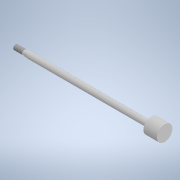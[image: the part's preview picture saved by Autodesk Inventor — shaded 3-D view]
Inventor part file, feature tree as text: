
AUTODESK INVENTOR PART (.ipt)
format: ipt  version: 2024.3 (Build 283343000, 343)  size: 141,824 bytes
history: native  units: mm
features: other x14, sketch x2, revolve x1, thread x1, extrude x1
ambient origin geometry x8: Origin, YZ Plane, XZ Plane, XY Plane, X Axis, Y Axis, Z Axis, Center Point
bodies: Solid1 (feature_tree)
feature tree (19):
  revolve  "Revolution1"  [1 undecoded]
  thread  "Thread1"  [1 undecoded]
  extrude  "Extrusion1"  [1 undecoded]
  other  "accessories_l_XY"
  other  "accessories_l_YZ"
  other  "accessories_l_ZX"
  other  "accessories_l_X"
  other  "accessories_l_Y"
  other  "accessories_l_Z"
  other  "accessories_l_Center"
  other  "rod_XY"
  other  "rod_YZ"
  other  "rod_ZX"
  other  "rod_X"
  other  "rod_Y"
  other  "rod_Z"
  other  "rod_Center"
  sketch  "Sketch_1"  dims[d0=360.0deg d1=18.233mm d2=0.0mm d3=6.0mm d4=0.0mm]
  sketch  "Sketch_3"
note: 3 required parameter values undecoded (feature->parameter linkage not recoverable at this tier; creation-order binding heuristic only, values carry confidence <= 0.55)